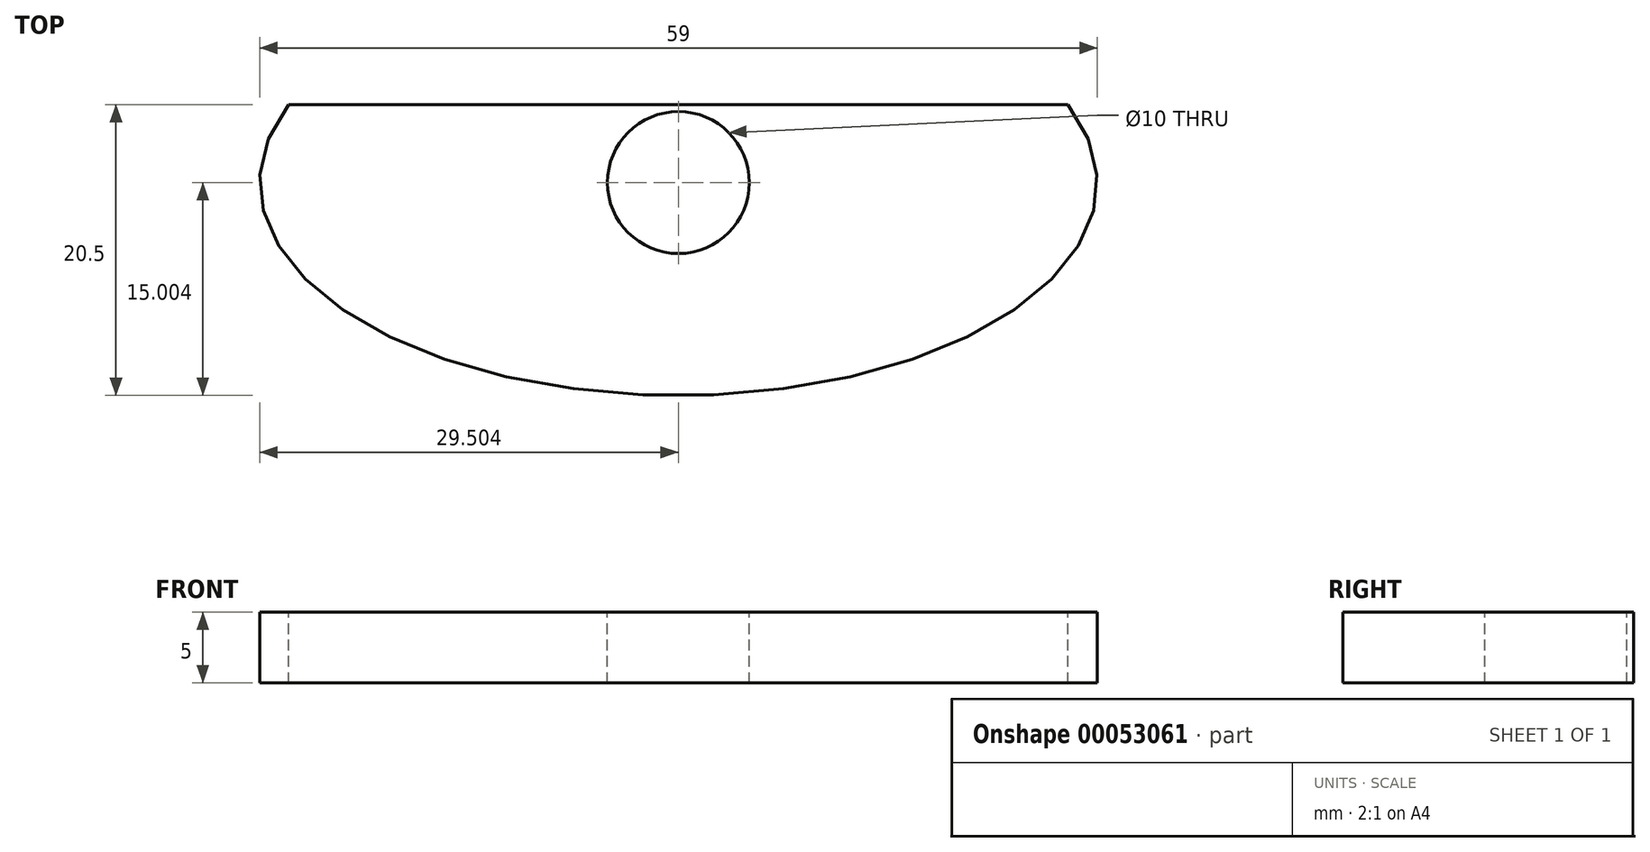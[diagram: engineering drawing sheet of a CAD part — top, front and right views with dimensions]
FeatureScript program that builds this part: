
annotation { "Feature Type Name" : "Feature", "Feature Type Description" : "" }
export const myFeature = defineFeature(function(context is Context, id is Id, definition is map)
    precondition{}
    {
        {
            var Q0;
            Q0=qCreatedBy(makeId("Top.planeOp"),FACE);
            var sketch = newSketch(context, id + "F0", { "sketchPlane" : qUnion([Q0])});
            skEllipse(sketch, "E0", {"center": v(-36.73, 20.36) * mm, "majorRadius": 29.5 * mm, "minorRadius": 15 * mm, "majorAxis": v(-1, 0)});
            skSolve(sketch);
        }
        {
            var Q0;
            {var subQ0=sQuery(id+"F0.wireOp",EDGE,"E0");var subQ1=sQuery(id+"F0.wireOp",EDGE,"aEvzKXr8-QTBp-xoGQ-6Xab-mmZP7m4J7e4N");var subQ2=makeQuery(id+"F0.imprint","INTERSECT",VERTEX,{"disambiguationData":[OD(0.0)],"derivedFrom":[subQ1,subQ0]});Q0=makeQuery(id+"F0.imprint","IMPRINT",FACE,{"disambiguationData":[TD([[makeQuery(id+"F0.imprint","IMPRINT",EDGE,{"disambiguationData":[TD([[subQ2,-1.0]])],"derivedFrom":subQ1}),1.0]])]});}
            var Q1;
            {var subQ0=sQuery(id+"F0.wireOp",EDGE,"E0");var subQ1=sQuery(id+"F0.wireOp",EDGE,"aEvzKXr8-QTBp-xoGQ-6Xab-mmZP7m4J7e4N");var subQ2=makeQuery(id+"F0.imprint","INTERSECT",VERTEX,{"disambiguationData":[OD(1.0)],"derivedFrom":[subQ1,subQ0]});Q1=makeQuery(id+"F0.imprint","IMPRINT",FACE,{"disambiguationData":[TD([[makeQuery(id+"F0.imprint","IMPRINT",EDGE,{"disambiguationData":[TD([[subQ2,1.0]])],"derivedFrom":subQ1}),-1.0]])]});}
            var Q2;
            {var subQ0=sQuery(id+"F0.wireOp",EDGE,"E0");var subQ1=sQuery(id+"F0.wireOp",EDGE,"aEvzKXr8-QTBp-xoGQ-6Xab-mmZP7m4J7e4N");var subQ2=makeQuery(id+"F0.imprint","INTERSECT",VERTEX,{"disambiguationData":[OD(0.0)],"derivedFrom":[subQ1,subQ0]});Q2=makeQuery(id+"F0.imprint","IMPRINT",FACE,{"disambiguationData":[TD([[makeQuery(id+"F0.imprint","IMPRINT",EDGE,{"disambiguationData":[TD([[subQ2,-1.0]])],"derivedFrom":subQ1}),-1.0]])]});}
            var Q3;
            Q3=makeQuery(id+"F0.imprint","IMPRINT",FACE,{"disambiguationData":[TD([[makeQuery(id+"F0.imprint","IMPRINT",EDGE,{"derivedFrom":sQuery(id+"F0.wireOp",EDGE,"E0")}),1.0]])]});
            extrude(context, id + "F1", {"entities" : qUnion([Q0, Q1, Q2, Q3]), "depth" : 5 * mm});
        }
        {
            var Q0;
            Q0=makeQuery(id+"F1.opExtrude","CAP_FACE",FACE,{"disambiguationData":[OSD([sQuery(id+"F0.wireOp",EDGE,"E0")])],"isStart":false});
            var sketch = newSketch(context, id + "F2", { "sketchPlane" : qUnion([Q0])});
            skCircle(sketch, "E1", {"center": v(-36.73, 20.36) * mm, "radius": 5 * mm});
            skSolve(sketch);
        }
        {
            var Q0;
            Q0=makeQuery(id+"F2.imprint","IMPRINT",FACE,{"disambiguationData":[TD([[makeQuery(id+"F2.imprint","IMPRINT",EDGE,{"derivedFrom":sQuery(id+"F2.wireOp",EDGE,"E1")}),1.0]])]});
            extrude(context, id + "F3", {"entities" : qUnion([Q0]), "operationType" : NewBodyOperationType.REMOVE, "oppositeDirection" : true, "depth" : 25 * mm});
        }
        {
            var Q0;
            Q0=makeQuery(id+"F1.opExtrude","CAP_FACE",FACE,{"disambiguationData":[OSD([sQuery(id+"F0.wireOp",EDGE,"E0")])],"isStart":false});
            var sketch = newSketch(context, id + "F4", { "sketchPlane" : qUnion([Q0])});
            skLineSegment(sketch, "E2", {"start": v(-64.17, 25.86) * mm, "end": v(-9.28, 25.86) * mm});
            skSolve(sketch);
        }
        {
            var Q0;
            {var subQ0=sQuery(id+"F4.wireOp",EDGE,"E2");Q0=makeQuery(id+"F4.imprint","IMPRINT",FACE,{"disambiguationData":[TD([[makeQuery(id+"F4.imprint","IMPRINT",EDGE,{"derivedFrom":subQ0}),1.0]])]});}
            extrude(context, id + "F5", {"entities" : qUnion([Q0]), "operationType" : NewBodyOperationType.REMOVE, "oppositeDirection" : true, "depth" : 25 * mm});
        }
    });
